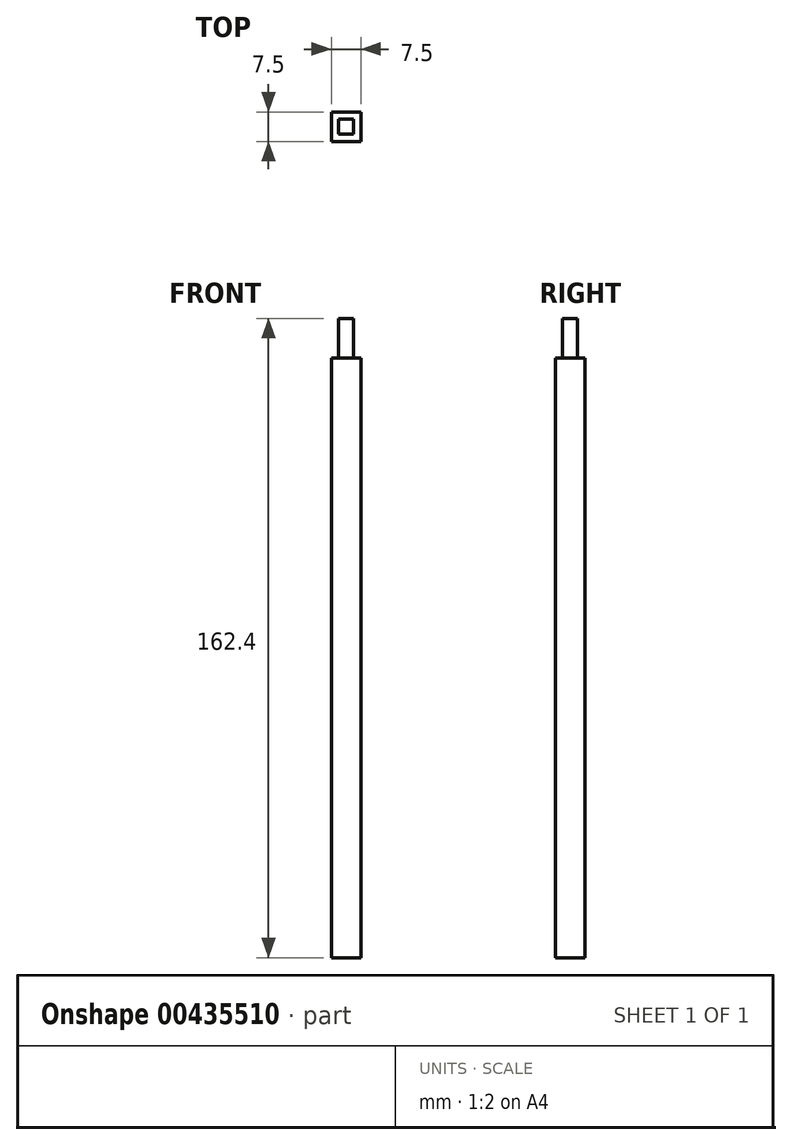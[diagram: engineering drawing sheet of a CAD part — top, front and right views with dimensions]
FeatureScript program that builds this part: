
annotation { "Feature Type Name" : "Feature", "Feature Type Description" : "" }
export const myFeature = defineFeature(function(context is Context, id is Id, definition is map)
    precondition{}
    {
        {
            var Q0;
            Q0=qCreatedBy(makeId("Top.planeOp"),FACE);
            var sketch = newSketch(context, id + "F0", { "sketchPlane" : qUnion([Q0])});
            skLineSegment(sketch, "E0.bottom", {"start": v(3.75, 3.75) * mm, "end": v(-3.75, 3.75) * mm});
            skLineSegment(sketch, "E0.top", {"start": v(3.75, -3.75) * mm, "end": v(-3.75, -3.75) * mm});
            skLineSegment(sketch, "E0.left", {"start": v(3.75, 3.75) * mm, "end": v(3.75, -3.75) * mm});
            skLineSegment(sketch, "E0.right", {"start": v(-3.75, 3.75) * mm, "end": v(-3.75, -3.75) * mm});
            skPoint(sketch, "E0.middle", {"position": v(0, 0) * mm});
            skSolve(sketch);
        }
        {
            var Q0;
            Q0 = qSketchRegion(id + "F0", true);
            extrude(context, id + "F1", {"entities" : qUnion([Q0]), "oppositeDirection" : true, "depth" : 152.4 * mm, "offsetDistance" : 25.4 * mm});
        }
        {
            var Q0;
            Q0=makeQuery(id+"F1.opExtrude","CAP_FACE",FACE,{"disambiguationData":[OSD([sQuery(id+"F0.wireOp",EDGE,"E0.bottom"),sQuery(id+"F0.wireOp",EDGE,"E0.top"),sQuery(id+"F0.wireOp",EDGE,"E0.left"),sQuery(id+"F0.wireOp",EDGE,"E0.right")])],"isStart":true});
            var sketch = newSketch(context, id + "F2", { "sketchPlane" : qUnion([Q0])});
            skLineSegment(sketch, "E1.bottom", {"start": v(1.9, -1.9) * mm, "end": v(-1.9, -1.9) * mm});
            skLineSegment(sketch, "E1.top", {"start": v(1.9, 1.9) * mm, "end": v(-1.9, 1.9) * mm});
            skLineSegment(sketch, "E1.left", {"start": v(1.9, -1.9) * mm, "end": v(1.9, 1.9) * mm});
            skLineSegment(sketch, "E1.right", {"start": v(-1.9, -1.9) * mm, "end": v(-1.9, 1.9) * mm});
            skPoint(sketch, "E1.middle", {"position": v(0, 0) * mm});
            skSolve(sketch);
        }
        {
            var Q0;
            Q0 = qSketchRegion(id + "F2", true);
            extrude(context, id + "F3", {"entities" : qUnion([Q0]), "operationType" : NewBodyOperationType.ADD, "depth" : 10 * mm, "offsetDistance" : 25 * mm});
        }
    });
